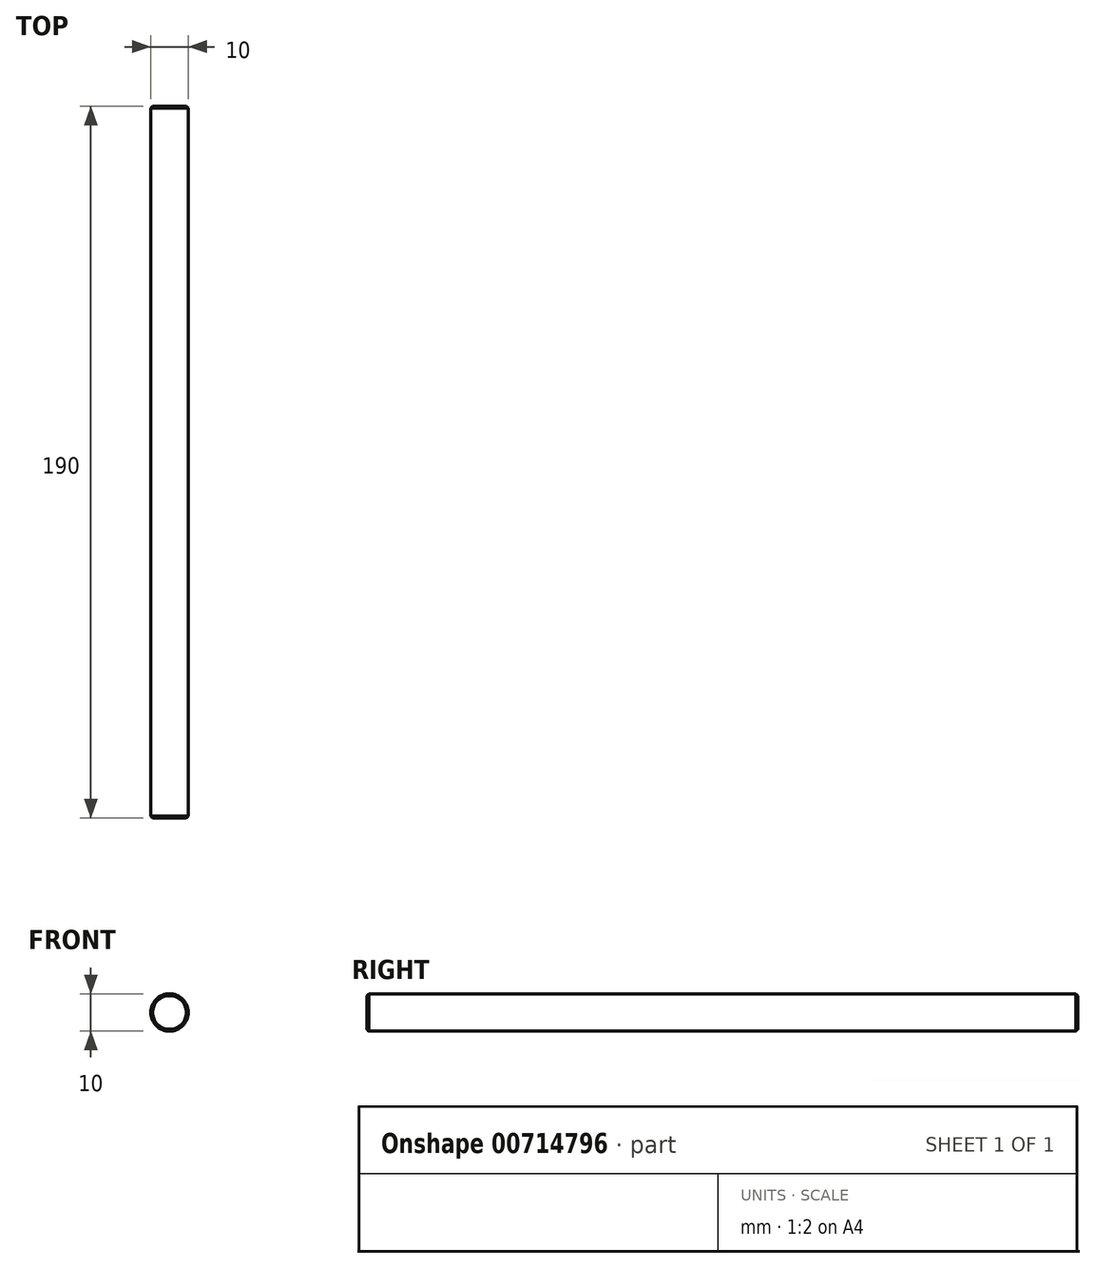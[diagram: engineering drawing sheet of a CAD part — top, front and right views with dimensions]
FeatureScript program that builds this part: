
annotation { "Feature Type Name" : "Feature", "Feature Type Description" : "" }
export const myFeature = defineFeature(function(context is Context, id is Id, definition is map)
    precondition{}
    {
        {
            var Q0;
            Q0=qCreatedBy(makeId("Front.planeOp"),FACE);
            var sketch = newSketch(context, id + "F0", { "sketchPlane" : qUnion([Q0])});
            skCircle(sketch, "E0", {"center": v(0, 0) * mm, "radius": 5 * mm});
            skSolve(sketch);
        }
        {
            var Q0;
            Q0 = qSketchRegion(id + "F0", true);
            extrude(context, id + "F1", {"entities" : qUnion([Q0]), "depth" : 190 * mm, "offsetDistance" : 25 * mm});
        }
        {
            var Q0;
            Q0=makeQuery(id+"F1.opExtrude","CAP_EDGE",EDGE,{"disambiguationData":[OSD([sQuery(id+"F0.wireOp",EDGE,"E0")])],"isStart":false});
            var Q1;
            Q1=makeQuery(id+"F1.opExtrude","CAP_EDGE",EDGE,{"disambiguationData":[OSD([sQuery(id+"F0.wireOp",EDGE,"E0")])],"isStart":true});
            chamfer(context, id + "F2", {"entities" : qUnion([Q0, Q1]), "width" : .5 * mm, "tangentPropagation" : true});
        }
    });
